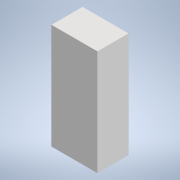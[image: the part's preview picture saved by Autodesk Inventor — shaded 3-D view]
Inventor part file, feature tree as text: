
AUTODESK INVENTOR PART (.ipt)
format: ipt  version: 2022.3 (Build 263350030, 350C)  size: 91,136 bytes
history: native  units: mm
features: extrude x1, sketch x1
ambient origin geometry x8: Origin, YZ Plane, XZ Plane, XY Plane, X Axis, Y Axis, Z Axis, Center Point
bodies: Solid1 (feature_tree)
feature tree (2):
  extrude  "Extrusion1"  Depth=78.0mm
  sketch  "Sketch1"  dims[d0=34.0mm d1=78.0mm d2=23.0mm d3=0.0mm]
